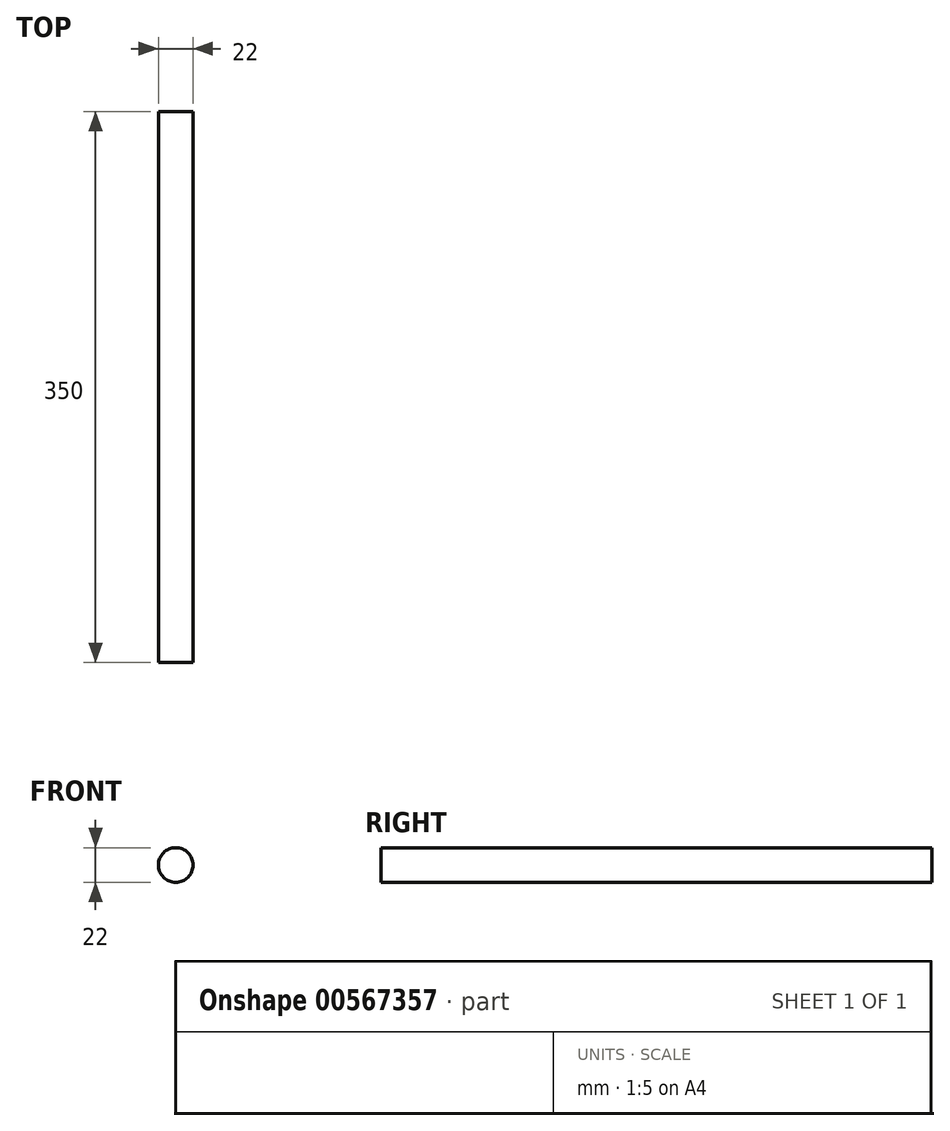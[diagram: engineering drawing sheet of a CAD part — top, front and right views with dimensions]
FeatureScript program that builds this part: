
annotation { "Feature Type Name" : "Feature", "Feature Type Description" : "" }
export const myFeature = defineFeature(function(context is Context, id is Id, definition is map)
    precondition{}
    {
        {
            var Q0;
            Q0=qCreatedBy(makeId("Front.planeOp"),FACE);
            var sketch = newSketch(context, id + "F0", { "sketchPlane" : qUnion([Q0])});
            skCircle(sketch, "E0", {"center": v(1.5, 0) * mm, "radius": 11 * mm});
            skSolve(sketch);
        }
        {
            var Q0;
            Q0 = qSketchRegion(id + "F0", true);
            extrude(context, id + "F1", {"entities" : qUnion([Q0]), "depth" : 350 * mm, "offsetDistance" : 25 * mm});
        }
    });
